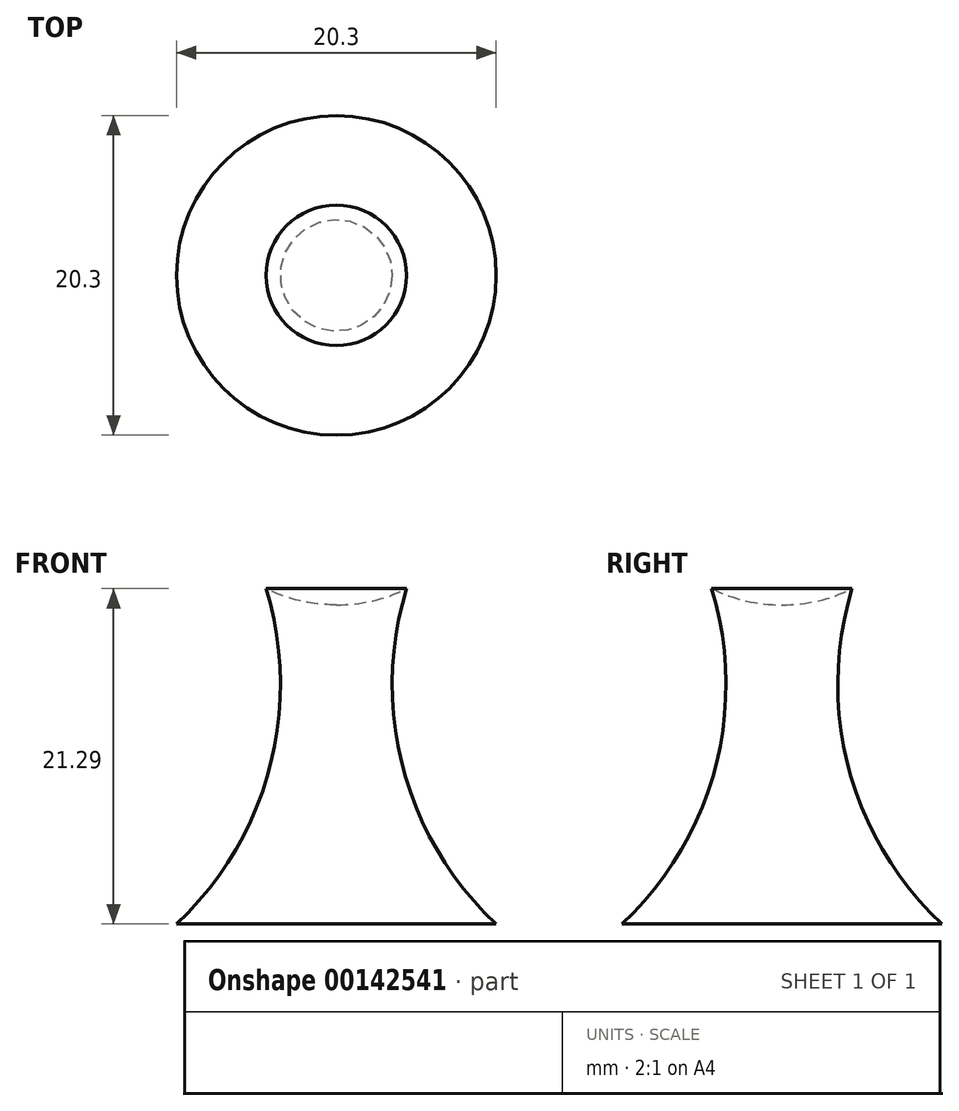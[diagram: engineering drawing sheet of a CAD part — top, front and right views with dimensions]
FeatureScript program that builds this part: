
annotation { "Feature Type Name" : "Feature", "Feature Type Description" : "" }
export const myFeature = defineFeature(function(context is Context, id is Id, definition is map)
    precondition{}
    {
        {
            var Q0;
            Q0=qCreatedBy(makeId("Front.planeOp"),FACE);
            var sketch = newSketch(context, id + "F0", { "sketchPlane" : qUnion([Q0])});
            skLineSegment(sketch, "E0", {"start": v(0, 0) * mm, "end": v(10.15, 0) * mm});
            skArc(sketch, "E1", {"start": v(4.46, 21.3) * mm, "mid": v(4.26, 9.83) * mm, "end": v(10.15, 0) * mm});
            skLineSegment(sketch, "E2.MirrorCS", {"start": v(0, 0) * mm, "end": v(-10.15, 0) * mm});
            skArc(sketch, "E3.MirrorCS", {"start": v(-4.46, 21.3) * mm, "mid": v(-4.26, 9.83) * mm, "end": v(-10.15, 0) * mm});
            skLineSegment(sketch, "E4", {"start": v(0, 40.54) * mm, "end": v(0, 0) * mm});
            skCircle(sketch, "E5", {"center": v(0, 30.4) * mm, "radius": 10.14 * mm});
            skSolve(sketch);
        }
        {
            var Q0;
            {var subQ0=sQuery(id+"F0.wireOp",EDGE,"E2.MirrorCS");Q0=makeQuery(id+"F0.imprint","IMPRINT",FACE,{"disambiguationData":[TD([[makeQuery(id+"F0.imprint","IMPRINT",EDGE,{"derivedFrom":subQ0}),-1.0]])]});}
            var Q1;
            {var subQ0=sQuery(id+"F0.wireOp",EDGE,"E5");var subQ1=sQuery(id+"F0.wireOp",EDGE,"E4");var subQ2=makeQuery(id+"F0.imprint","INTERSECT",VERTEX,{"disambiguationData":[OD(0.0)],"derivedFrom":[subQ1,subQ0]});Q1=makeQuery(id+"F0.imprint","IMPRINT",FACE,{"disambiguationData":[TD([[makeQuery(id+"F0.imprint","IMPRINT",EDGE,{"disambiguationData":[TD([[subQ2,-1.0]])],"derivedFrom":subQ1}),-1.0]])]});}
            var Q2;
            Q2=sQuery(id+"F0.wireOp",EDGE,"E4");
            revolve(context, id + "F1", {"entities" : qUnion([Q0, Q1]), "axis" : qUnion([Q2]), "revolveType" : RevolveType.ONE_DIRECTION, "angle" : 360 * degree});
        }
    });
